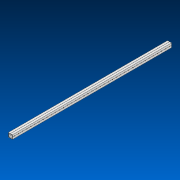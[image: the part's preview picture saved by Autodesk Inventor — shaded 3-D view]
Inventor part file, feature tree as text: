
AUTODESK INVENTOR PART (.ipt)
format: ipt  version: 2022.2 (Build 262287000, 287)  size: 822,784 bytes
history: native  units: in
note: dims shown in document units (in); Inventor stores cm internally (conversion verified against a paired STEP export)
features: other x39, extrude x1, pattern_linear x1, sketch x1, pattern_circular x1
ambient origin geometry x8: Origin, YZ Plane, XZ Plane, XY Plane, X Axis, Y Axis, Z Axis, Center Point
bodies: Solid1 (feature_tree)
feature tree (43):
  extrude  "Extrusion1"  Depth=1.0in
  other  "Work Axis1"
  pattern_linear  "Rectangular Pattern1"  Spacing1=0.0in  [1 undecoded]
  sketch  "Sketch1"  dims[d0=1.0in d1=20.0in d2=0.0in d3=15.3543in d5=1.0in]
  other  "Work Axis2"
  other  "Work Axis3"
  other  "Work Axis4"
  other  "Work Axis5"
  other  "Work Axis6"
  other  "Work Axis7"
  other  "Work Axis8"
  other  "Work Axis9"
  other  "Work Axis10"
  other  "Work Axis11"
  other  "Work Axis12"
  other  "Work Axis13"
  other  "Work Axis14"
  other  "Work Axis15"
  other  "Work Axis16"
  other  "Work Axis17"
  other  "Work Axis18"
  other  "Work Axis19"
  other  "Work Axis20"
  other  "Work Axis21"
  other  "Work Axis22"
  other  "Work Axis23"
  other  "Work Axis24"
  other  "Work Axis25"
  other  "Work Axis26"
  other  "Work Axis27"
  other  "Work Axis28"
  other  "Work Axis29"
  other  "Work Axis30"
  other  "Work Axis31"
  other  "Work Axis32"
  other  "Work Axis33"
  other  "Work Axis34"
  other  "Work Axis35"
  other  "Work Axis36"
  other  "Work Axis37"
  other  "Work Axis38"
  other  "Work Axis39"
  pattern_circular  "CirPattern2"
note: 1 required parameter value undecoded (feature->parameter linkage not recoverable at this tier; creation-order binding heuristic only, values carry confidence <= 0.55)
